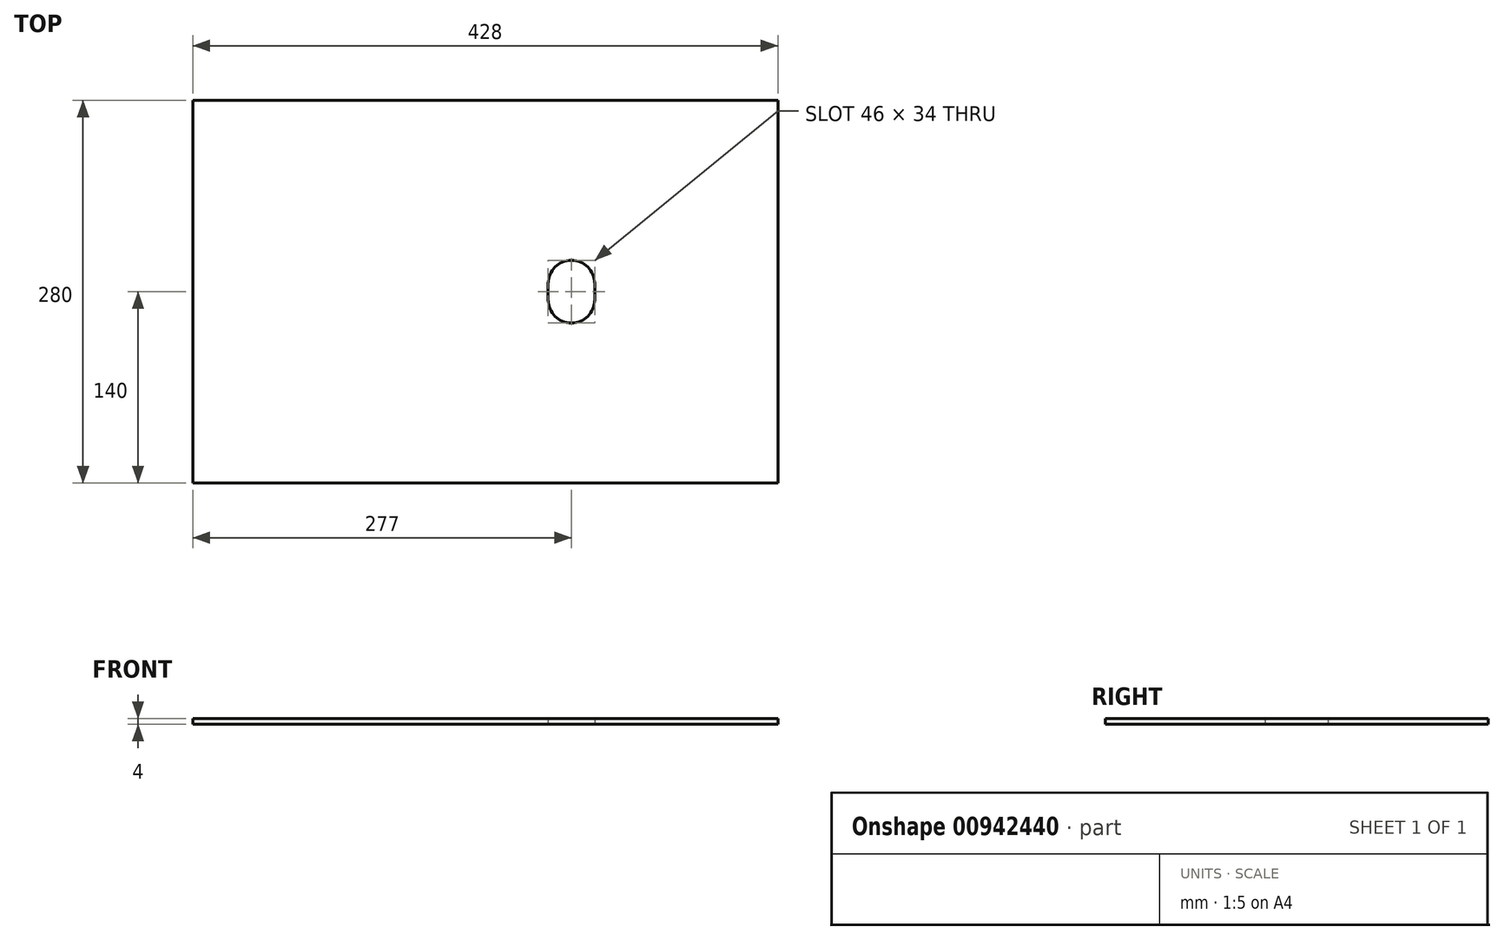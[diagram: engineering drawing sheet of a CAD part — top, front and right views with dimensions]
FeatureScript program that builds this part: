
annotation { "Feature Type Name" : "Feature", "Feature Type Description" : "" }
export const myFeature = defineFeature(function(context is Context, id is Id, definition is map)
    precondition{}
    {
        {
            var Q0;
            Q0=qCreatedBy(makeId("Top.planeOp"),FACE);
            var sketch = newSketch(context, id + "F0", { "sketchPlane" : qUnion([Q0])});
            skLineSegment(sketch, "E0.bottom", {"start": v(-214, 140) * mm, "end": v(214, 140) * mm});
            skLineSegment(sketch, "E0.top", {"start": v(-214, -140) * mm, "end": v(214, -140) * mm});
            skLineSegment(sketch, "E0.left", {"start": v(-214, 140) * mm, "end": v(-214, -140) * mm});
            skLineSegment(sketch, "E0.right", {"start": v(214, 140) * mm, "end": v(214, -140) * mm});
            skArc(sketch, "E1", {"start": v(80, 6) * mm, "mid": v(63, 23) * mm, "end": v(46, 6) * mm});
            skArc(sketch, "E2", {"start": v(46, -6) * mm, "mid": v(63, -23) * mm, "end": v(80, -6) * mm});
            skLineSegment(sketch, "E3", {"start": v(46, 6) * mm, "end": v(46, -6) * mm});
            skLineSegment(sketch, "E4", {"start": v(80, 6) * mm, "end": v(80, -6) * mm});
            skSolve(sketch);
        }
        {
            var Q0;
            Q0 = qSketchRegion(id + "F0", true);
            extrude(context, id + "F1", {"entities" : qUnion([Q0]), "depth" : 4 * mm, "offsetDistance" : 25 * mm});
        }
    });
